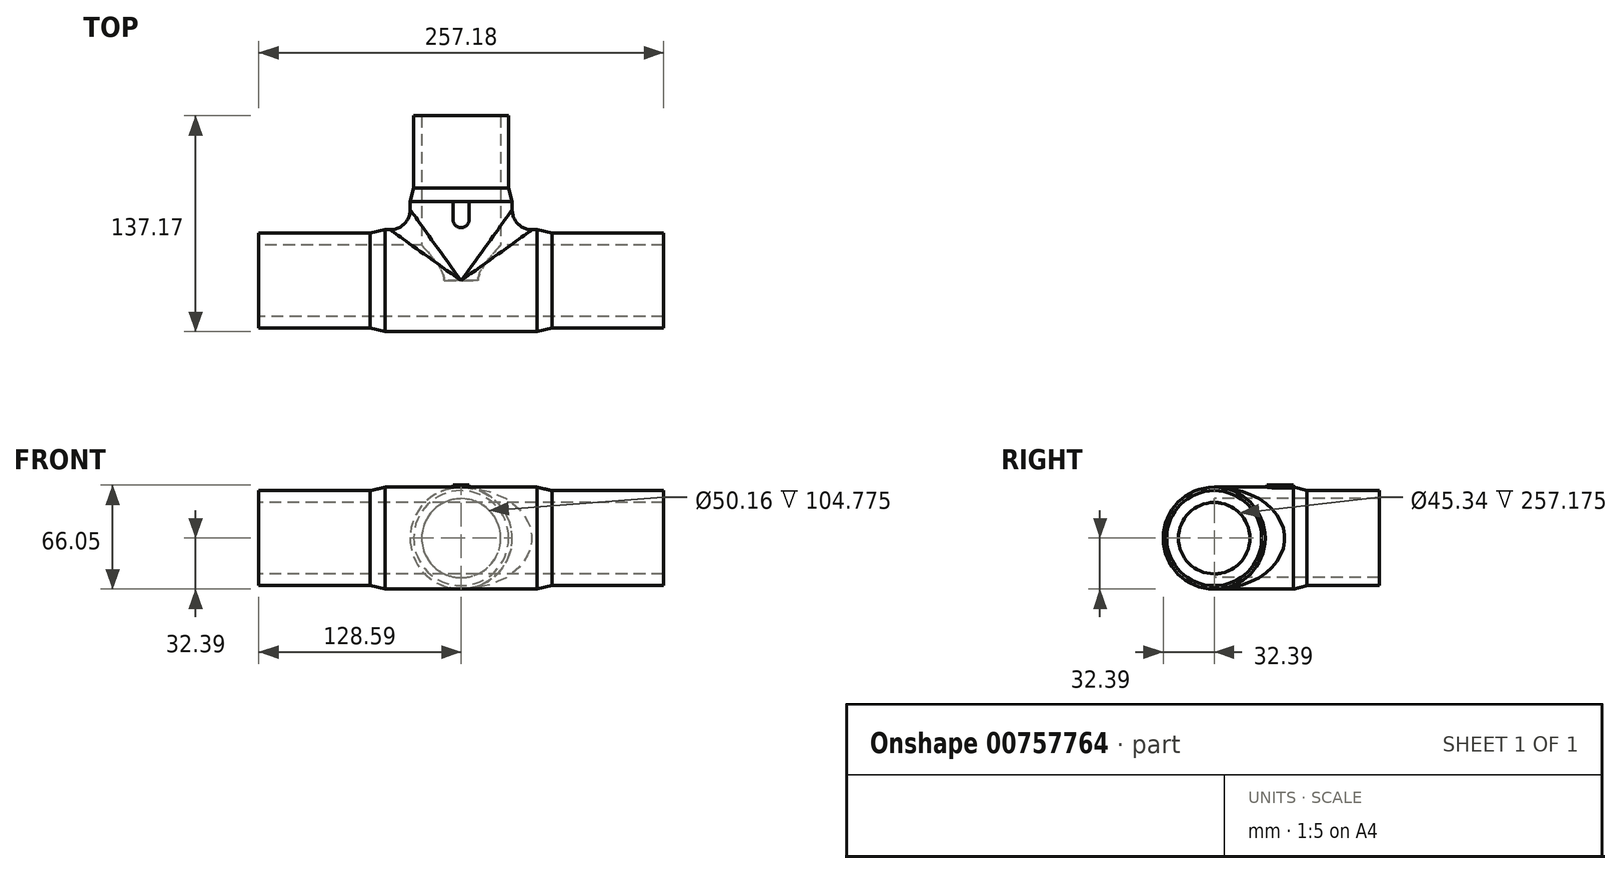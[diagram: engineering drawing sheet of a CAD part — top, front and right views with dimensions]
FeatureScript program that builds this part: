
annotation { "Feature Type Name" : "Feature", "Feature Type Description" : "" }
export const myFeature = defineFeature(function(context is Context, id is Id, definition is map)
    precondition{}
    {
        {
            var Q0;
            Q0=qCreatedBy(makeId("Top.planeOp"),FACE);
            var sketch = newSketch(context, id + "F0", { "sketchPlane" : qUnion([Q0])});
            skLineSegment(sketch, "E0", {"start": v(0, 0) * mm, "end": v(77.4, 0) * mm, "construction": true});
            skLineSegment(sketch, "E1", {"start": v(-128.59, 22.67) * mm, "end": v(128.59, 22.67) * mm});
            skLineSegment(sketch, "E2", {"start": v(128.59, 30.16) * mm, "end": v(57.91, 30.16) * mm});
            skLineSegment(sketch, "E3", {"start": v(-128.59, 30.16) * mm, "end": v(-128.59, 22.67) * mm});
            skLineSegment(sketch, "E4", {"start": v(-57.91, 30.16) * mm, "end": v(-48.26, 32.39) * mm});
            skLineSegment(sketch, "E5", {"start": v(-48.26, 32.38) * mm, "end": v(48.26, 32.39) * mm});
            skLineSegment(sketch, "E6", {"start": v(48.26, 32.39) * mm, "end": v(57.91, 30.16) * mm});
            skLineSegment(sketch, "E7.trimOffspring", {"start": v(-57.91, 30.16) * mm, "end": v(-128.59, 30.16) * mm});
            skLineSegment(sketch, "E8", {"start": v(0, 32.38) * mm, "end": v(0, 0) * mm, "construction": true});
            skPoint(sketch, "E9.orphan", {"position": v(56.25, 16.86) * mm});
            skLineSegment(sketch, "E10", {"start": v(128.59, 30.16) * mm, "end": v(128.59, 22.67) * mm});
            skSolve(sketch);
        }
        {
            var Q0;
            Q0 = qSketchRegion(id + "F0", true);
            var Q1;
            Q1=sQuery(id+"F0.wireOp",EDGE,"E0");
            revolve(context, id + "F1", {"surfaceOperationType" : NewSurfaceOperationType.NEW, "entities" : qUnion([Q0]), "axis" : qUnion([Q1]), "revolveType" : RevolveType.FULL});
        }
        {
            var Q0;
            Q0=qCreatedBy(makeId("Top.planeOp"),FACE);
            var sketch = newSketch(context, id + "F2", { "sketchPlane" : qUnion([Q0])});
            skLineSegment(sketch, "E11", {"start": v(0, 0) * mm, "end": v(0, 99.35) * mm, "construction": true});
            skLineSegment(sketch, "E12", {"start": v(32.39, 0) * mm, "end": v(32.39, 50.42) * mm});
            skLineSegment(sketch, "E13", {"start": v(32.38, 50.42) * mm, "end": v(30.16, 58.8) * mm});
            skLineSegment(sketch, "E14", {"start": v(30.16, 58.8) * mm, "end": v(30.16, 104.78) * mm});
            skLineSegment(sketch, "E15", {"start": v(30.16, 104.78) * mm, "end": v(25.08, 104.78) * mm});
            skLineSegment(sketch, "E16", {"start": v(25.08, 104.78) * mm, "end": v(25.08, 0) * mm});
            skLineSegment(sketch, "E17", {"start": v(25.08, 0) * mm, "end": v(32.39, 0) * mm});
            skLineSegment(sketch, "E18", {"start": v(52.58, -32.38) * mm, "end": v(-52.58, -32.38) * mm, "construction": true});
            skSolve(sketch);
        }
        {
            var Q0;
            Q0 = qSketchRegion(id + "F2", true);
            var Q1;
            Q1=sQuery(id+"F2.wireOp",EDGE,"E11");
            revolve(context, id + "F3", {"operationType" : NewBodyOperationType.ADD, "surfaceOperationType" : NewSurfaceOperationType.NEW, "entities" : qUnion([Q0]), "axis" : qUnion([Q1]), "revolveType" : RevolveType.FULL});
        }
        {
            var Q0;
            Q0=makeQuery(id+"F3.boolean.opBoolean","INTERSECT",EDGE,{"disambiguationData":[OD(1.0)],"derivedFrom":[makeQuery(id+"F1.opRevolve","SWEPT_FACE",FACE,{"disambiguationData":[OSD([sQuery(id+"F0.wireOp",EDGE,"E5")])]}),makeQuery(id+"F3.opRevolve","SWEPT_FACE",FACE,{"disambiguationData":[OSD([sQuery(id+"F2.wireOp",EDGE,"E12")])]})]});
            var Q1;
            Q1=makeQuery(id+"F3.boolean.opBoolean","INTERSECT",EDGE,{"disambiguationData":[OD(0.0)],"derivedFrom":[makeQuery(id+"F1.opRevolve","SWEPT_FACE",FACE,{"disambiguationData":[OSD([sQuery(id+"F0.wireOp",EDGE,"E5")])]}),makeQuery(id+"F3.opRevolve","SWEPT_FACE",FACE,{"disambiguationData":[OSD([sQuery(id+"F2.wireOp",EDGE,"E12")])]})]});
            fillet(context, id + "F4", {"entities" : qUnion([Q0, Q1]), "radius" : 12.7 * mm, "tangentPropagation" : true, "allowEdgeOverflow" : false});
        }
        {
            var Q0;
            Q0=qCreatedBy(makeId("Top.planeOp"),FACE);
            cPlane(context, id + "F5", {"entities" : qUnion([Q0]), "cplaneType" : CPlaneType.OFFSET, "offset" : 32.38 * mm, "width" : 152.4 * mm, "height" : 152.4 * mm});
        }
        {
            var Q0;
            Q0=qCreatedBy(id+"F5.planeOp",FACE);
            var sketch = newSketch(context, id + "F6", { "sketchPlane" : qUnion([Q0])});
            skArc(sketch, "E19", {"start": v(-5.08, 38.74) * mm, "mid": v(0, 33.66) * mm, "end": v(5.08, 38.74) * mm});
            skLineSegment(sketch, "E20", {"start": v(51.08, -32.38) * mm, "end": v(-51.08, -32.38) * mm, "construction": true});
            skLineSegment(sketch, "E21", {"start": v(-5.08, 38.74) * mm, "end": v(-5.08, 50.42) * mm});
            skLineSegment(sketch, "E22", {"start": v(-5.08, 50.42) * mm, "end": v(5.08, 50.42) * mm});
            skLineSegment(sketch, "E23", {"start": v(5.08, 50.42) * mm, "end": v(5.08, 38.74) * mm});
            skLineSegment(sketch, "E24", {"start": v(0, 38.74) * mm, "end": v(0, 50.42) * mm, "construction": true});
            skSolve(sketch);
        }
        {
            var Q0;
            Q0 = qSketchRegion(id + "F6", true);
            extrude(context, id + "F7", {"entities" : qUnion([Q0]), "operationType" : NewBodyOperationType.ADD, "depth" : 1.27 * mm, "offsetDistance" : 25.4 * mm, "hasSecondDirection" : true, "secondDirectionBound" : BoundingType.UP_TO_NEXT, "secondDirectionOppositeDirection" : true, "secondDirectionDepth" : 25.4 * mm});
        }
        {
            var Q0;
            Q0=makeQuery(id+"F1.opRevolve","SWEPT_FACE",FACE,{"disambiguationData":[OSD([sQuery(id+"F0.wireOp",EDGE,"E10")])]});
            var sketch = newSketch(context, id + "F8", { "sketchPlane" : qUnion([Q0])});
            skCircle(sketch, "E25.0", {"center": v(0, 0) * mm, "radius": 22.67 * mm});
            skSolve(sketch);
        }
        {
            var Q0;
            Q0 = qSketchRegion(id + "F8", true);
            extrude(context, id + "F9", {"entities" : qUnion([Q0]), "operationType" : NewBodyOperationType.REMOVE, "endBound" : BoundingType.THROUGH_ALL, "oppositeDirection" : true, "depth" : 25.4 * mm, "offsetDistance" : 25.4 * mm});
        }
        {
            var Q0;
            Q0=makeQuery(id+"F3.opRevolve","SWEPT_FACE",FACE,{"disambiguationData":[OSD([sQuery(id+"F2.wireOp",EDGE,"E15")])]});
            var sketch = newSketch(context, id + "F10", { "sketchPlane" : qUnion([Q0])});
            skCircle(sketch, "E26.0", {"center": v(0, 0) * mm, "radius": 25.08 * mm});
            skSolve(sketch);
        }
        {
            var Q0;
            Q0 = qSketchRegion(id + "F10", true);
            var Q1;
            Q1=makeQuery(id+"F9.boolean.opBoolean","MERGE",FACE,{"derivedFrom":[makeQuery(id+"F1.opRevolve","SWEPT_FACE",FACE,{"disambiguationData":[OSD([sQuery(id+"F0.wireOp",EDGE,"E1")])]}),makeQuery(id+"F9.opExtrude","SWEPT_FACE",FACE,{"disambiguationData":[OSD([sQuery(id+"F8.wireOp",EDGE,"E25.0")])]})]});
            extrude(context, id + "F11", {"entities" : qUnion([Q0]), "operationType" : NewBodyOperationType.REMOVE, "oppositeDirection" : true, "depth" : 104.77 * mm, "endBoundEntityFace" : qUnion([Q1]), "offsetDistance" : 25.4 * mm});
        }
    });
